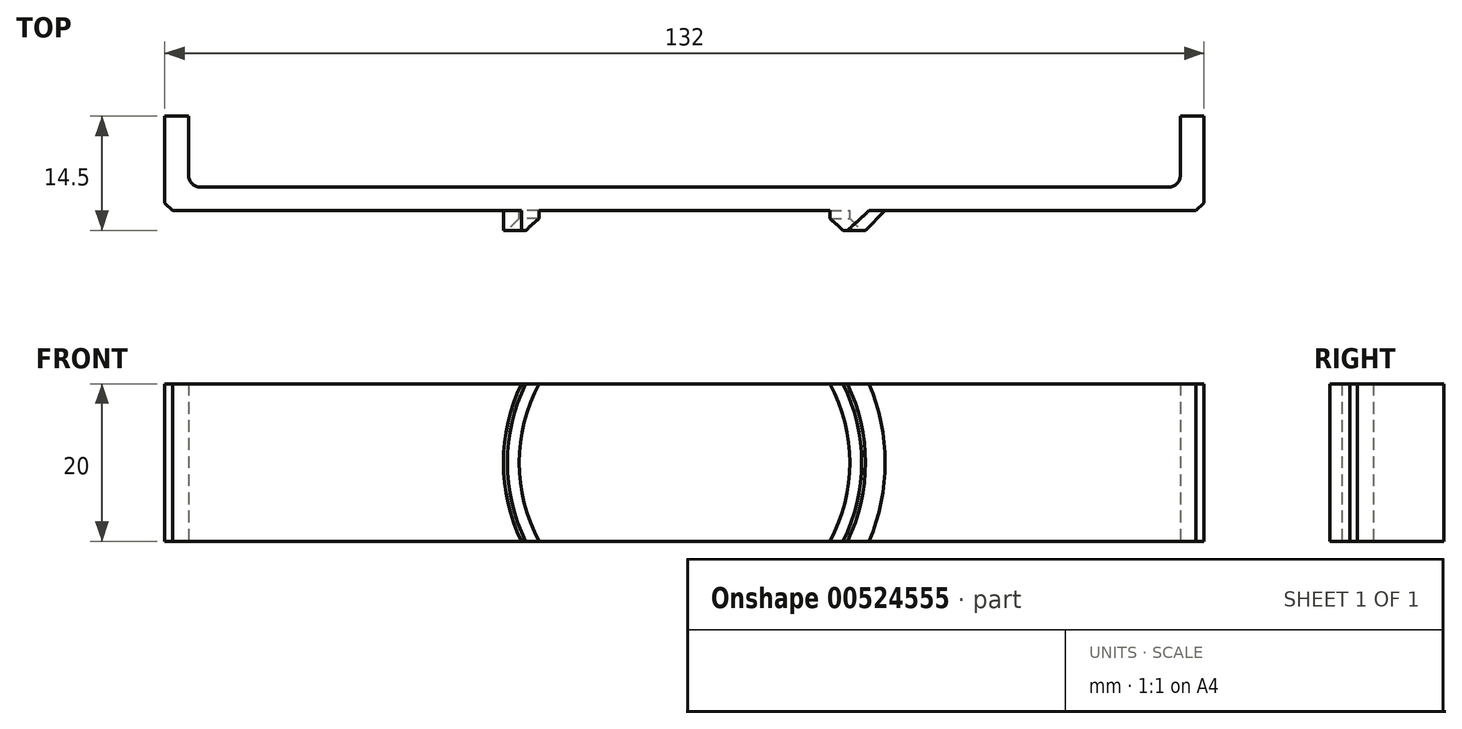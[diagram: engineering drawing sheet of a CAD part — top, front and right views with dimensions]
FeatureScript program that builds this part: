
annotation { "Feature Type Name" : "Feature", "Feature Type Description" : "" }
export const myFeature = defineFeature(function(context is Context, id is Id, definition is map)
    precondition{}
    {
        {
            var Q0;
            Q0=qCreatedBy(makeId("Top.planeOp"),FACE);
            var sketch = newSketch(context, id + "F0", { "sketchPlane" : qUnion([Q0])});
            skLineSegment(sketch, "E0", {"start": v(-63, 0) * mm, "end": v(63, 0) * mm});
            skLineSegment(sketch, "E1", {"start": v(-63, 0) * mm, "end": v(-63, 9) * mm});
            skLineSegment(sketch, "E2", {"start": v(-63, 9) * mm, "end": v(-66, 9) * mm});
            skLineSegment(sketch, "E3", {"start": v(-66, 9) * mm, "end": v(-66, -3) * mm});
            skLineSegment(sketch, "E4", {"start": v(-66, -3) * mm, "end": v(66, -3) * mm});
            skLineSegment(sketch, "E5", {"start": v(66, -3) * mm, "end": v(66, 9) * mm});
            skLineSegment(sketch, "E6", {"start": v(66, 9) * mm, "end": v(63, 9) * mm});
            skLineSegment(sketch, "E7", {"start": v(63, 9) * mm, "end": v(63, 0) * mm});
            skSolve(sketch);
        }
        {
            var Q0;
            Q0=makeQuery(id+"F0.imprint","IMPRINT",FACE,{"disambiguationData":[TD([[makeQuery(id+"F0.imprint","IMPRINT",EDGE,{"derivedFrom":sQuery(id+"F0.wireOp",EDGE,"E0")}),-1.0]])]});
            extrude(context, id + "F1", {"entities" : qUnion([Q0]), "endBound" : BoundingType.SYMMETRIC, "depth" : 20 * mm, "offsetDistance" : 25 * mm});
        }
        {
            var Q0;
            Q0=makeQuery(id+"F1.opExtrude","SWEPT_FACE",FACE,{"disambiguationData":[OSD([sQuery(id+"F0.wireOp",EDGE,"E4")])]});
            var sketch = newSketch(context, id + "F2", { "sketchPlane" : qUnion([Q0])});
            skArc(sketch, "E8", {"start": v(-18.47, 10) * mm, "mid": v(-21, 0) * mm, "end": v(-18.47, -10) * mm});
            skArc(sketch, "E9", {"start": v(-20.71, 10) * mm, "mid": v(-23, 0) * mm, "end": v(-20.71, -10) * mm});
            skLineSegment(sketch, "E10", {"start": v(-20.71, 10) * mm, "end": v(-18.47, 10) * mm});
            skLineSegment(sketch, "E11", {"start": v(18.47, 10) * mm, "end": v(20.71, 10) * mm});
            skLineSegment(sketch, "E12", {"start": v(-20.71, -10) * mm, "end": v(-18.47, -10) * mm});
            skLineSegment(sketch, "E13", {"start": v(20.71, -10) * mm, "end": v(18.47, -10) * mm});
            skArc(sketch, "E14.trimOffspring", {"start": v(18.47, -10) * mm, "mid": v(21, 0) * mm, "end": v(18.47, 10) * mm});
            skArc(sketch, "E15.trimOffspring", {"start": v(20.71, -10) * mm, "mid": v(23, 0) * mm, "end": v(20.71, 10) * mm});
            skSolve(sketch);
        }
        {
            var Q0;
            Q0=makeQuery(id+"F2.imprint","IMPRINT",FACE,{"disambiguationData":[TD([[makeQuery(id+"F2.imprint","IMPRINT",EDGE,{"derivedFrom":sQuery(id+"F2.wireOp",EDGE,"E8")}),-1.0]])]});
            var Q1;
            Q1=makeQuery(id+"F2.imprint","IMPRINT",FACE,{"disambiguationData":[TD([[makeQuery(id+"F2.imprint","IMPRINT",EDGE,{"derivedFrom":sQuery(id+"F2.wireOp",EDGE,"E11")}),-1.0]])]});
            extrude(context, id + "F3", {"entities" : qUnion([Q0, Q1]), "operationType" : NewBodyOperationType.ADD, "depth" : 2.5 * mm, "offsetDistance" : 25 * mm});
        }
        {
            var Q0;
            Q0=makeQuery(id+"F3.opExtrude","CAP_EDGE",EDGE,{"disambiguationData":[OSD([sQuery(id+"F2.wireOp",EDGE,"E8")])],"isStart":false});
            var Q1;
            Q1=makeQuery(id+"F3.opExtrude","CAP_EDGE",EDGE,{"disambiguationData":[OSD([sQuery(id+"F2.wireOp",EDGE,"E14.trimOffspring")])],"isStart":false});
            chamfer(context, id + "F4", {"entities" : qUnion([Q0, Q1]), "width" : 1.5 * mm, "tangentPropagation" : true});
        }
        {
            var Q0;
            Q0=makeQuery(id+"F3.opExtrude","CAP_EDGE",EDGE,{"disambiguationData":[OSD([sQuery(id+"F2.wireOp",EDGE,"E9")])],"isStart":true});
            var Q1;
            Q1=makeQuery(id+"F3.opExtrude","CAP_EDGE",EDGE,{"disambiguationData":[OSD([sQuery(id+"F2.wireOp",EDGE,"E15.trimOffspring")])],"isStart":true});
            chamfer(context, id + "F5", {"entities" : qUnion([Q0, Q1]), "width" : 2.5 * mm, "tangentPropagation" : true});
        }
        {
            var Q0;
            Q0=makeQuery(id+"F1.opExtrude","SWEPT_EDGE",EDGE,{"disambiguationData":[OSD([sQuery(id+"F0.wireOp",EDGE,"E3"),sQuery(id+"F0.wireOp",EDGE,"E4")])]});
            var Q1;
            Q1=makeQuery(id+"F1.opExtrude","SWEPT_EDGE",EDGE,{"disambiguationData":[OSD([sQuery(id+"F0.wireOp",EDGE,"E4"),sQuery(id+"F0.wireOp",EDGE,"E5")])]});
            chamfer(context, id + "F6", {"entities" : qUnion([Q0, Q1]), "width" : 1 * mm, "tangentPropagation" : true});
        }
        {
            var Q0;
            Q0=makeQuery(id+"F1.opExtrude","SWEPT_EDGE",EDGE,{"disambiguationData":[OSD([sQuery(id+"F0.wireOp",EDGE,"E0"),sQuery(id+"F0.wireOp",EDGE,"E7")])]});
            var Q1;
            Q1=makeQuery(id+"F1.opExtrude","SWEPT_EDGE",EDGE,{"disambiguationData":[OSD([sQuery(id+"F0.wireOp",EDGE,"E0"),sQuery(id+"F0.wireOp",EDGE,"E1")])]});
            fillet(context, id + "F7", {"entities" : qUnion([Q0, Q1]), "radius" : 1.5 * mm, "tangentPropagation" : true, "allowEdgeOverflow" : false});
        }
    });
